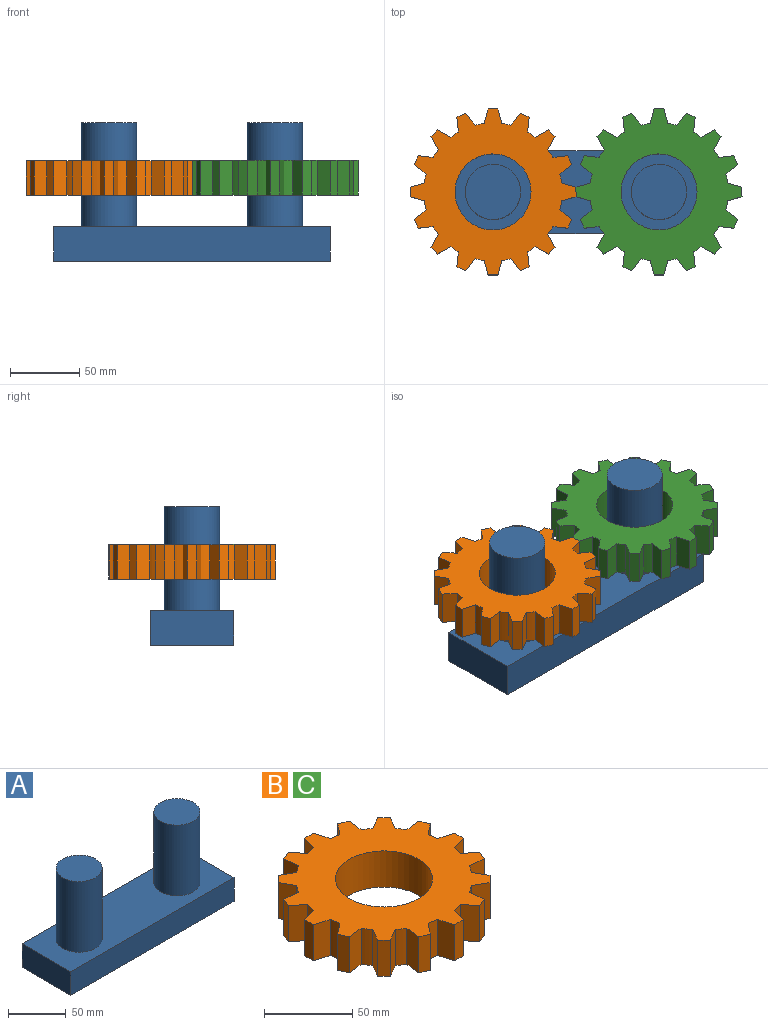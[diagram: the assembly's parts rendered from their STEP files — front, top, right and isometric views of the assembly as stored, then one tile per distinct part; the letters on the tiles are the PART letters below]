
ASSEMBLY  parts=3 mates=1
PART A: 10 faces, bbox 200x60x100 mm
  f0: plane 200x25mm, normal (0,1,0), area 5000mm2, adj f1,f3,f4,f5
  f1: plane 60x25mm, normal (-1,0,0), area 1500mm2, adj f0,f2,f4,f5
  f2: plane 200x25mm, normal (0,-1,0), area 5000mm2, adj f1,f3,f4,f5
  f3: plane 60x25mm, normal (1,0,0), area 1500mm2, adj f0,f2,f4,f5
  f4: plane 200x60mm, normal (0,0,-1), area 12000mm2, adj f0,f1,f2,f3
  f5: plane 200x60mm, normal (0,0,1), area 9486.7mm2, adj f0,f1,f2,f3,f6,f8
  f6: cylinder r=20mm len=75mm, axis (0,0,-1), area 9424.8mm2, adj f5,f7
  f7: plane 40x40mm, normal (0,0,1), area 1256.6mm2, adj f6
  f8: cylinder r=20mm len=75mm, axis (0,0,-1), area 9424.8mm2, adj f5,f9
  f9: plane 40x40mm, normal (0,0,1), area 1256.6mm2, adj f8
PART B: 67 faces, bbox 120x120x25 mm
  f0: plane 25x10.78mm, normal (-0.99,-0.11,0), area 271.2mm2, adj f1,f63,f65,f66
  f1: cylinder r=50mm len=25mm, axis (0,0,-1), area 165mm2, adj f0,f2,f65,f66
  f2: plane 25x9.49mm, normal (0.48,0.88,0), area 271.2mm2, adj f1,f3,f65,f66
  f3: plane 25x4.95mm, normal (-0.71,0.71,0), area 175mm2, adj f2,f4,f65,f66
  f4: plane 25x9.49mm, normal (-0.88,-0.48,0), area 271.2mm2, adj f3,f5,f65,f66
  f5: cylinder r=50mm len=25mm, axis (0,0,-1), area 165mm2, adj f4,f6,f65,f66
  f6: plane 25x10.78mm, normal (0.11,0.99,0), area 271.2mm2, adj f5,f7,f65,f66
  f7: plane 25x6.47mm, normal (-0.92,0.38,0), area 175mm2, adj f6,f8,f65,f66
  f8: plane 25x8.48mm, normal (-0.62,-0.78,0), area 271.2mm2, adj f7,f9,f65,f66
  f9: cylinder r=50mm len=25mm, axis (0,0,-1), area 165mm2, adj f8,f10,f65,f66
  f10: plane 25x10.42mm, normal (-0.28,0.96,0), area 271.2mm2, adj f9,f11,f65,f66
  f11: plane 25x7mm, normal (-1,0,0), area 175mm2, adj f10,f12,f65,f66
  f12: plane 25x10.42mm, normal (-0.28,-0.96,0), area 271.2mm2, adj f11,f13,f65,f66
  f13: cylinder r=50mm len=25mm, axis (0,0,-1), area 165mm2, adj f12,f14,f65,f66
  f14: plane 25x8.48mm, normal (-0.62,0.78,0), area 271.2mm2, adj f13,f15,f65,f66
  f15: plane 25x6.47mm, normal (-0.92,-0.38,0), area 175mm2, adj f14,f16,f65,f66
  f16: plane 25x10.78mm, normal (0.11,-0.99,0), area 271.2mm2, adj f15,f17,f65,f66
  f17: cylinder r=50mm len=25mm, axis (0,0,-1), area 165mm2, adj f16,f18,f65,f66
  f18: plane 25x9.49mm, normal (-0.88,0.48,0), area 271.2mm2, adj f17,f19,f65,f66
  f19: plane 25x4.95mm, normal (-0.71,-0.71,0), area 175mm2, adj f18,f20,f65,f66
  f20: plane 25x9.49mm, normal (0.48,-0.88,0), area 271.2mm2, adj f19,f21,f65,f66
  f21: cylinder r=50mm len=25mm, axis (0,0,-1), area 165mm2, adj f20,f22,f65,f66
  f22: plane 25x10.78mm, normal (-0.99,0.11,0), area 271.2mm2, adj f21,f23,f65,f66
  f23: plane 25x6.47mm, normal (-0.38,-0.92,0), area 175mm2, adj f22,f24,f65,f66
  f24: plane 25x8.48mm, normal (0.78,-0.62,0), area 271.2mm2, adj f23,f25,f65,f66
  f25: cylinder r=50mm len=25mm, axis (0,0,-1), area 165mm2, adj f24,f26,f65,f66
  f26: plane 25x10.42mm, normal (-0.96,-0.28,0), area 271.2mm2, adj f25,f27,f65,f66
  f27: plane 25x7mm, normal (0,-1,0), area 175mm2, adj f26,f28,f65,f66
  f28: plane 25x10.42mm, normal (0.96,-0.28,0), area 271.2mm2, adj f27,f29,f65,f66
  f29: cylinder r=50mm len=25mm, axis (0,0,-1), area 165mm2, adj f28,f30,f65,f66
  f30: plane 25x8.48mm, normal (-0.78,-0.62,0), area 271.2mm2, adj f29,f31,f65,f66
  f31: plane 25x6.47mm, normal (0.38,-0.92,0), area 175mm2, adj f30,f32,f65,f66
  f32: plane 25x10.78mm, normal (0.99,0.11,0), area 271.2mm2, adj f31,f33,f65,f66
  f33: cylinder r=50mm len=25mm, axis (0,0,-1), area 165mm2, adj f32,f34,f65,f66
  f34: plane 25x9.49mm, normal (-0.48,-0.88,0), area 271.2mm2, adj f33,f35,f65,f66
  f35: plane 25x4.95mm, normal (0.71,-0.71,0), area 175mm2, adj f34,f36,f65,f66
  f36: plane 25x9.49mm, normal (0.88,0.48,0), area 271.2mm2, adj f35,f37,f65,f66
  f37: cylinder r=50mm len=25mm, axis (0,0,-1), area 165mm2, adj f36,f38,f65,f66
  f38: plane 25x10.78mm, normal (-0.11,-0.99,0), area 271.2mm2, adj f37,f39,f65,f66
  f39: plane 25x6.47mm, normal (0.92,-0.38,0), area 175mm2, adj f38,f40,f65,f66
  f40: plane 25x8.48mm, normal (0.62,0.78,0), area 271.2mm2, adj f39,f41,f65,f66
  f41: cylinder r=50mm len=25mm, axis (0,0,-1), area 165mm2, adj f40,f42,f65,f66
  f42: plane 25x10.42mm, normal (0.28,-0.96,0), area 271.2mm2, adj f41,f43,f65,f66
  f43: plane 25x7mm, normal (1,0,0), area 175mm2, adj f42,f44,f65,f66
  f44: plane 25x10.42mm, normal (0.28,0.96,0), area 271.2mm2, adj f43,f45,f65,f66
  f45: cylinder r=50mm len=25mm, axis (0,0,-1), area 165mm2, adj f44,f46,f65,f66
  f46: plane 25x8.48mm, normal (0.62,-0.78,0), area 271.2mm2, adj f45,f47,f65,f66
  f47: plane 25x6.47mm, normal (0.92,0.38,0), area 175mm2, adj f46,f48,f65,f66
  f48: plane 25x10.78mm, normal (-0.11,0.99,0), area 271.2mm2, adj f47,f49,f65,f66
  f49: cylinder r=50mm len=25mm, axis (0,0,-1), area 165mm2, adj f48,f50,f65,f66
  f50: plane 25x9.49mm, normal (0.88,-0.48,0), area 271.2mm2, adj f49,f51,f65,f66
  f51: plane 25x4.95mm, normal (0.71,0.71,0), area 175mm2, adj f50,f52,f65,f66
  f52: plane 25x9.49mm, normal (-0.48,0.88,0), area 271.2mm2, adj f51,f53,f65,f66
  f53: cylinder r=50mm len=25mm, axis (0,0,-1), area 165mm2, adj f52,f54,f65,f66
  f54: plane 25x10.78mm, normal (0.99,-0.11,0), area 271.2mm2, adj f53,f55,f65,f66
  f55: plane 25x6.47mm, normal (0.38,0.92,0), area 175mm2, adj f54,f56,f65,f66
  f56: plane 25x8.48mm, normal (-0.78,0.62,0), area 271.2mm2, adj f55,f57,f65,f66
  f57: cylinder r=50mm len=25mm, axis (0,0,-1), area 165mm2, adj f56,f58,f65,f66
  f58: plane 25x10.42mm, normal (0.96,0.28,0), area 271.2mm2, adj f57,f59,f65,f66
  f59: plane 25x7mm, normal (0,1,0), area 175mm2, adj f58,f60,f65,f66
  f60: plane 25x10.42mm, normal (-0.96,0.28,0), area 271.2mm2, adj f59,f61,f65,f66
  f61: cylinder r=50mm len=25mm, axis (0,0,-1), area 165mm2, adj f60,f62,f65,f66
  f62: plane 25x8.48mm, normal (0.78,0.62,0), area 271.2mm2, adj f61,f63,f65,f66
  f63: plane 25x6.47mm, normal (-0.38,0.92,0), area 175mm2, adj f0,f62,f65,f66
  f64: cylinder r=27.5mm len=55mm, axis (0,0,-1), area 4319.7mm2, adj f65,f66
  f65: plane 120x120mm, normal (0,0,1), area 7087.2mm2, adj f0,f1,f2,f3,f4,f5,f6,f7
  f66: plane 120x120mm, normal (0,0,-1), area 7087.2mm2, adj f0,f1,f2,f3,f4,f5,f6,f7
PART C: same geometry as B
PLACE A rot(axis=(0,0,1),0deg) t=(-33.03,138.49,42.32)mm
PLACE B rot(axis=(0,0,1),0deg) t=(-93.03,138.49,64.93)mm
PLACE C rot(axis=(0,0,1),0deg) t=(26.97,138.49,65.12)mm
MATE slider A.f6 <-> B.f1  axis (0,0,-1) through (-93.03,138.49,79.82)mm
